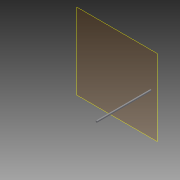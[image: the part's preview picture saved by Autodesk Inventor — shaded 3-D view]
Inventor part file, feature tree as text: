
AUTODESK INVENTOR PART (.ipt)
format: ipt  version: 2013 (Build 170138000, 138)  size: 64,512 bytes
history: native  units: in
note: dims shown in document units (in); Inventor stores cm internally (conversion verified against a paired STEP export)
features: plane x1, extrude x1, sketch x1
ambient origin geometry x8: Origin, YZ Plane, XZ Plane, XY Plane, X Axis, Y Axis, Z Axis, Center Point
bodies: Solid1 (feature_tree)
feature tree (3):
  plane  "Work Plane2"
  extrude  "Extrusion1"  Depth=16.0in TaperAngle=0.0deg
  sketch  "Sketch1"  dims[d0=0.5in d1=16.0in d2=0.0in]
